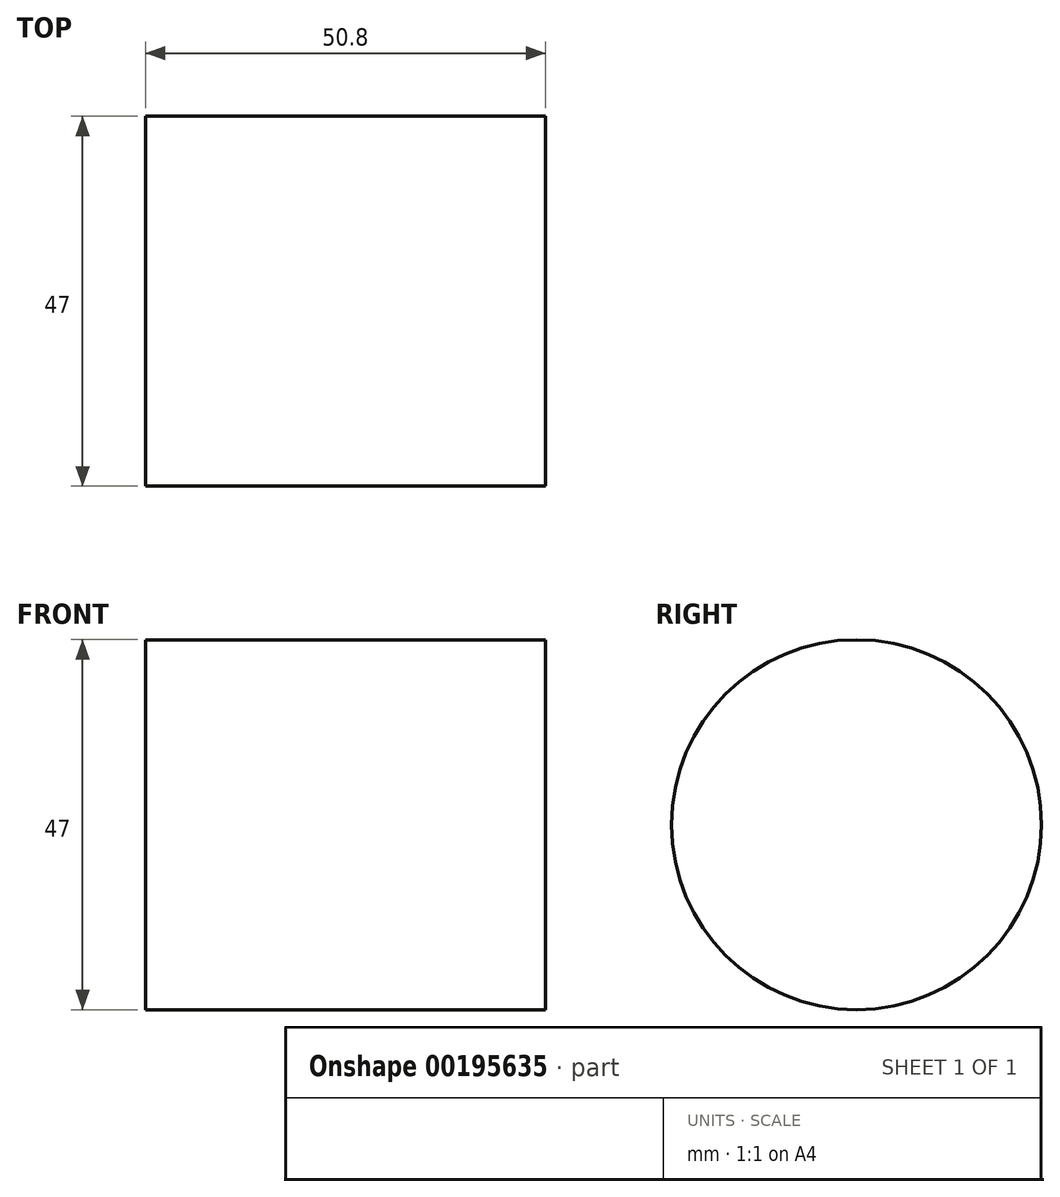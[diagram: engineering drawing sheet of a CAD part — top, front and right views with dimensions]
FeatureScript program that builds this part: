
annotation { "Feature Type Name" : "Feature", "Feature Type Description" : "" }
export const myFeature = defineFeature(function(context is Context, id is Id, definition is map)
    precondition{}
    {
        {
            var Q0;
            Q0=qCreatedBy(makeId("Right.planeOp"),FACE);
            var sketch = newSketch(context, id + "F0", { "sketchPlane" : qUnion([Q0])});
            skCircle(sketch, "E0", {"center": v(0, 0) * mm, "radius": 23.5 * mm});
            skSolve(sketch);
        }
        {
            var Q0;
            Q0=makeQuery(id+"F0.imprint","IMPRINT",FACE,{"disambiguationData":[TD([[makeQuery(id+"F0.imprint","IMPRINT",EDGE,{"derivedFrom":sQuery(id+"F0.wireOp",EDGE,"E0")}),1.0]])]});
            var Q1;
            Q1=sQuery(id+"F0.wireOp",EDGE,"E0");
            extrude(context, id + "F1", {"entities" : qUnion([Q0]), "surfaceEntities" : qUnion([Q1]), "depth" : 25.4 * mm, "hasSecondDirection" : true, "secondDirectionOppositeDirection" : true, "secondDirectionDepth" : 25.4 * mm});
        }
    });
